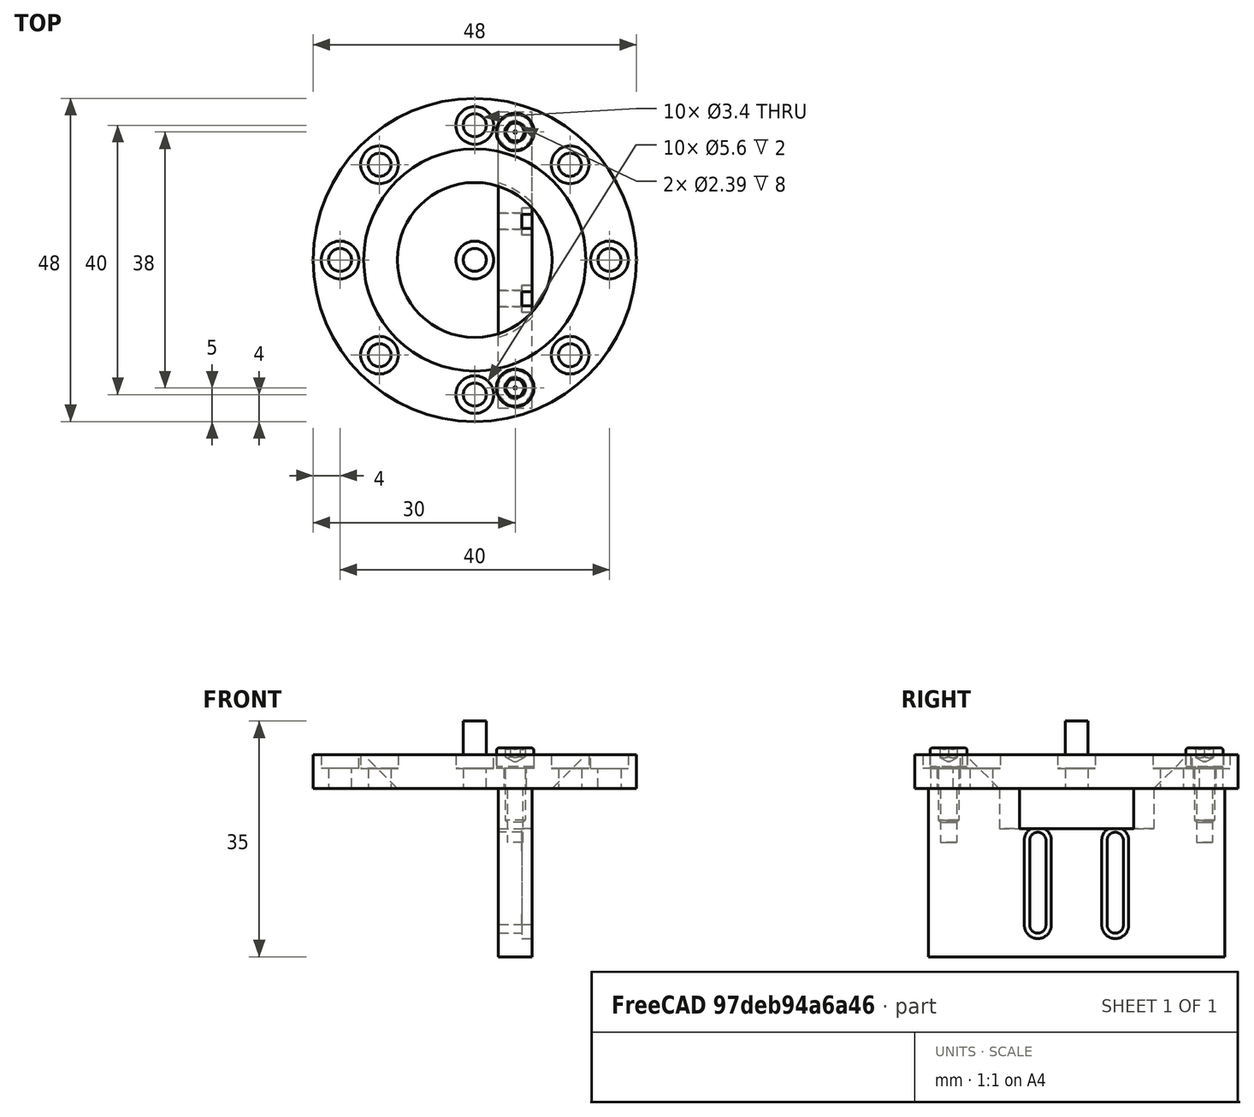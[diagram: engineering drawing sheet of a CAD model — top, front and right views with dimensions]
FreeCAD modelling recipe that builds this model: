
FCSTD DOCUMENT  (FreeCAD 0.22R0.21.2)
Label: PhilipsXL30_AligningRing
License: All rights reserved
LicenseURL: http://en.wikipedia.org/wiki/All_rights_reserved
objects: TechDraw::DrawViewDimension×43, Part::Cylinder×18, Part::MultiFuse×9, TechDraw::DrawProjGroupItem×8, Part::Cut×7, Part::Box×5, Part::FeaturePython×3, TechDraw::DrawSVGTemplate×3, TechDraw::DrawViewSection×3, TechDraw::DrawPage×3, Part::Feature×2, TechDraw::DrawProjGroup×2, TechDraw::DrawViewPart×2, Part::Cone×1
note: 107 computed .brp shape members not serialized (recipe doc carries the construction recipe); baked Part::Feature solids carry a one-line shape summary decoded from their .brp

FEATURE [Part::Cone] Cone001
  Angle = 360
  AttacherType = Attacher::AttachEngine3D
  Height = 20
  Placement = pos=(0,0,-5) rot=(0,0,1;0rad)
  Radius1 = 6.5
  Radius2 = 26.5
FEATURE [Part::Cylinder] Cylinder
  Angle = 360
  AttacherType = Attacher::AttachEngine3D
  FirstAngle = 0
  Height = 5
  Radius = 24
  SecondAngle = 0
FEATURE [Part::Cut] Cut
  Base = -> Cylinder
  Tool = -> Cone001
FEATURE [Part::Box] Box  label="Cube"
  AttacherType = Attacher::AttachEngine3D
  Height = 25
  Length = 5
  Placement = pos=(3.5,-22,-25) rot=(0,0,1;0rad)
  Width = 44
FEATURE [Part::Cylinder] Cylinder001
  Angle = 360
  AttacherType = Attacher::AttachEngine3D
  FirstAngle = 0
  Height = 10
  Radius = 1.2
  SecondAngle = 0
FEATURE [Part::Cylinder] Cylinder002
  Angle = 360
  AttacherType = Attacher::AttachEngine3D
  FirstAngle = 0
  Height = 10
  Placement = pos=(12.6,0,0) rot=(0,0,1;0rad)
  Radius = 1.2
  SecondAngle = 0
FEATURE [Part::Box] Box001  label="Cube001"
  AttacherType = Attacher::AttachEngine3D
  Height = 10
  Length = 12.5
  Placement = pos=(0,-1.2,0) rot=(0,0,1;0rad)
  Width = 2.4
FEATURE [Part::MultiFuse] Fusion  label="Langloch"
  Placement = pos=(0,5.75,-7.7) rot=(0,1,0;1.5708rad)
  Shapes = -> [Box001,Cylinder001,Cylinder002]
FEATURE [Part::Box] Box002  label="Cube002"
  AttacherType = Attacher::AttachEngine3D
  Height = 10
  Length = 12.5
  Placement = pos=(0,-1.2,0) rot=(0,0,1;0rad)
  Width = 2.4
FEATURE [Part::Cylinder] Cylinder003
  Angle = 360
  AttacherType = Attacher::AttachEngine3D
  FirstAngle = 0
  Height = 10
  Radius = 1.2
  SecondAngle = 0
FEATURE [Part::Cylinder] Cylinder004
  Angle = 360
  AttacherType = Attacher::AttachEngine3D
  FirstAngle = 0
  Height = 10
  Placement = pos=(12.6,0,0) rot=(0,0,1;0rad)
  Radius = 1.2
  SecondAngle = 0
FEATURE [Part::MultiFuse] Fusion001  label="Langloch001"
  Placement = pos=(0,-5.75,-7.7) rot=(0,1,0;1.5708rad)
  Shapes = -> [Box002,Cylinder003,Cylinder004]
FEATURE [Part::MultiFuse] Fusion002
  Shapes = -> [Fusion001,Fusion]
FEATURE [Part::Cut] Cut001
  Base = -> Box
  Tool = -> Fusion002
FEATURE [Part::Cylinder] Cylinder005
  Angle = 360
  AttacherType = Attacher::AttachEngine3D
  FirstAngle = 0
  Height = 17
  Placement = pos=(0,0,-6) rot=(0,0,1;0rad)
  Radius = 12
  SecondAngle = 0
FEATURE [Part::Cut] Cut002
  Base = -> Cut001
  Tool = -> Cylinder005
FEATURE [Part::FeaturePython] Screw  label="M3x8-Screw"  # Fasteners workbench fastener (typed FeaturePython)
  Placement = pos=(6,19,3) rot=(0,0,1;0rad)
  diameter = 4
  invert = false
  leftHanded = false
  length = 2
  lengthCustom = 8
  matchOuter = false
  offset = 0
  thread = false
  type = 48
FEATURE [Part::FeaturePython] Screw001  label="M3x8-Screw001"  # Fasteners workbench fastener (typed FeaturePython)
  Placement = pos=(6,-19,3) rot=(0,0,1;0rad)
  diameter = 4
  invert = false
  leftHanded = false
  length = 2
  lengthCustom = 8
  matchOuter = false
  offset = 0
  thread = false
  type = 48
FEATURE [Part::Cylinder] Cylinder006
  Angle = 360
  AttacherType = Attacher::AttachEngine3D
  FirstAngle = 0
  Height = 10
  Placement = pos=(6,19,-8) rot=(0,0,1;0rad)
  Radius = 1.195
  SecondAngle = 0
FEATURE [Part::Cylinder] Cylinder007
  Angle = 360
  AttacherType = Attacher::AttachEngine3D
  FirstAngle = 0
  Height = 10
  Placement = pos=(6,-19,-8) rot=(0,0,1;0rad)
  Radius = 1.195
  SecondAngle = 0
FEATURE [Part::MultiFuse] Fusion003
  Shapes = -> [Cylinder006,Cylinder007]
FEATURE [Part::Cut] Cut003  label="Kickeraligner_01"
  Base = -> Cut002
  Tool = -> Fusion003
FEATURE [Part::Cylinder] Cylinder008
  Angle = 360
  AttacherType = Attacher::AttachEngine3D
  FirstAngle = 0
  Height = 10
  Placement = pos=(6,19,0) rot=(0,0,1;0rad)
  Radius = 1.7
  SecondAngle = 0
FEATURE [Part::Cylinder] Cylinder009
  Angle = 360
  AttacherType = Attacher::AttachEngine3D
  FirstAngle = 0
  Height = 10
  Placement = pos=(6,-19,0) rot=(0,0,1;0rad)
  Radius = 1.7
  SecondAngle = 0
FEATURE [Part::Cylinder] Cylinder010
  Angle = 360
  AttacherType = Attacher::AttachEngine3D
  FirstAngle = 0
  Height = 2
  Placement = pos=(6,19,3) rot=(0,0,1;0rad)
  Radius = 2.8
  SecondAngle = 0
FEATURE [Part::Cylinder] Cylinder011
  Angle = 360
  AttacherType = Attacher::AttachEngine3D
  FirstAngle = 0
  Height = 2
  Placement = pos=(6,-19,3) rot=(0,0,1;0rad)
  Radius = 2.8
  SecondAngle = 0
FEATURE [Part::MultiFuse] Fusion004
  Shapes = -> [Cylinder008,Cylinder009,Cylinder010,Cylinder011]
FEATURE [Part::Cut] Cut004
  Base = -> Cut
  Tool = -> Fusion004
FEATURE [Part::Cylinder] Cylinder012
  Angle = 360
  AttacherType = Attacher::AttachEngine3D
  FirstAngle = 0
  Height = 2
  Placement = pos=(0,0,3) rot=(0,0,1;0rad)
  Radius = 2.8
  SecondAngle = 0
FEATURE [Part::Cylinder] Cylinder013
  Angle = 360
  AttacherType = Attacher::AttachEngine3D
  FirstAngle = 0
  Height = 10
  Radius = 1.7
  SecondAngle = 0
FEATURE [Part::MultiFuse] Fusion005
  Shapes = -> [Cylinder013,Cylinder012]
FEATURE [Part::FeaturePython] Array  # Draft array (typed FeaturePython)
  AlwaysSyncPlacement = false
  Angle = 360
  ArrayType = 2
  Axis = (0,0,1)
  Base = -> Fusion005
  Center = (0,0,0)
  Count = 9
  ExpandArray = false
  Fuse = false
  IntervalAxis = (0,0,0)
  IntervalX = (100,0,0)
  IntervalY = (0,100,0)
  IntervalZ = (0,0,100)
  NumberCircles = 2
  NumberPolar = 5
  NumberX = 2
  NumberY = 2
  NumberZ = 1
  PlacementList = 9 placements: [(0,0,0),(-20,0,0),(-14.1421,-14.1421,0),(-4.44089e-15,-20,0),(14.1421,-14.1421,0),(20,-2.44929e-15,0),(14.1421,14.1421,0),(4.44089e-15,20,0),(-14.1421,14.1421,0)]
  RadialDistance = 20
  ScaleList = (9) [(1,1,1),(1,1,1),(1,1,1),(1,1,1),(1,1,1),(1,1,1),(1,1,1),(1,1,1),(1,1,1)]
  Symmetry = 1
  TangentialDistance = 15
FEATURE [Part::Cut] Cut005  label="AligningRing"
  Base = -> Cut004
  Tool = -> Array
FEATURE [Part::Feature] Cut005_solid  label="AligningRing (Solid)"
  shape: bbox 48 x 48 x 5 mm, 34 faces (baked)
FEATURE [TechDraw::DrawSVGTemplate] Template
  EditableTexts = Designed_by_Name=Thomas Spielauer; FC-Date=2024-06-04; FC-SC=mm; FC-Title=XL30 Column Alignment Ring; Subtitle=Subtitle
  Height = 210
  Orientation = 1
  Template = <path>
  Width = 297
FEATURE [TechDraw::DrawProjGroupItem] ProjItem  label="Front"
  CoarseView = false
  Direction = (0,0,1)
  Focus = 100
  HardHidden = false
  IsoCount = 0
  IsoHidden = false
  IsoVisible = false
  LockPosition = true
  Perspective = false
  Rotation = 0
  RotationVector = (0,1,0)
  Scale = 2
  ScaleType = 2
  ScrubCount = 0
  SeamHidden = false
  SeamVisible = false
  SmoothHidden = false
  SmoothVisible = true
  Source = -> [Cut005]
  Type = 0
  X = 0
  XDirection = (0,1,0)
  Y = 0
FEATURE [TechDraw::DrawProjGroupItem] ProjItem001  label="Rear"
  CoarseView = false
  Direction = (0,0,-1)
  Focus = 100
  HardHidden = false
  IsoCount = 0
  IsoHidden = false
  IsoVisible = false
  LockPosition = false
  Perspective = false
  Rotation = 0
  RotationVector = (1,0,0)
  Scale = 2
  ScaleType = 2
  ScrubCount = 0
  SeamHidden = false
  SeamVisible = false
  SmoothHidden = false
  SmoothVisible = true
  Source = -> [Cut005]
  Type = 3
  X = 136
  XDirection = (0,-1,0)
  Y = 0
FEATURE [TechDraw::DrawProjGroupItem] ProjItem002  label="Left"
  CoarseView = false
  Direction = (0,-1,1e-16)
  Focus = 100
  HardHidden = false
  IsoCount = 0
  IsoHidden = false
  IsoVisible = false
  LockPosition = false
  Perspective = false
  Rotation = 0
  RotationVector = (1,0,0)
  Scale = 2
  ScaleType = 2
  ScrubCount = 0
  SeamHidden = false
  SeamVisible = false
  SmoothHidden = false
  SmoothVisible = true
  Source = -> [Cut005]
  Type = 1
  X = 68
  XDirection = (0,1e-16,1)
  Y = 0
FEATURE [TechDraw::DrawProjGroup] ProjGroup
  Anchor = -> ProjItem
  AutoDistribute = true
  LockPosition = false
  ProjectionType = 0
  Rotation = 0
  Scale = 2
  ScaleType = 1
  Source = -> [Cut005]
  Views = -> [ProjItem,ProjItem001,ProjItem002]
  X = 75.1959
  Y = 130.904
  spacingX = 15
  spacingY = 15
FEATURE [TechDraw::DrawViewDimension] Dimension
  AngleOverride = false
  Arbitrary = false
  ArbitraryTolerances = false
  EqualTolerance = true
  ExtensionAngle = 0
  FormatSpec = %.2w
  FormatSpecOverTolerance = %+.2w
  FormatSpecUnderTolerance = %+.2w
  Inverted = false
  LineAngle = 0
  LockPosition = false
  MeasureType = 1
  OverTolerance = 0
  References2D = -> [ProjItem002]
  Rotation = 0
  ScaleType = 0
  TheoreticalExact = false
  Type = 1
  UnderTolerance = 0
  X = 14.6766
  Y = 64.1241
FEATURE [TechDraw::DrawViewDimension] Dimension001
  AngleOverride = false
  Arbitrary = false
  ArbitraryTolerances = false
  EqualTolerance = true
  ExtensionAngle = 0
  FormatSpec = ⌀%.2w
  FormatSpecOverTolerance = %+.2w
  FormatSpecUnderTolerance = %+.2w
  Inverted = false
  LineAngle = 0
  LockPosition = false
  MeasureType = 1
  OverTolerance = 0
  References2D = -> [ProjItem001]
  Rotation = 0
  ScaleType = 0
  TheoreticalExact = false
  Type = 5
  UnderTolerance = 0
  X = 14.4966
  Y = 59.5959
FEATURE [TechDraw::DrawViewDimension] Dimension002
  AngleOverride = false
  Arbitrary = false
  ArbitraryTolerances = false
  EqualTolerance = true
  ExtensionAngle = 0
  FormatSpec = ⌀%.2w
  FormatSpecOverTolerance = %+.2w
  FormatSpecUnderTolerance = %+.2w
  Inverted = false
  LineAngle = 0
  LockPosition = false
  MeasureType = 1
  OverTolerance = 0
  References2D = -> [ProjItem001]
  Rotation = 0
  ScaleType = 0
  TheoreticalExact = false
  Type = 5
  UnderTolerance = 0
  X = 30.1939
  Y = 53.0714
FEATURE [TechDraw::DrawViewDimension] Dimension003
  AngleOverride = false
  Arbitrary = false
  ArbitraryTolerances = false
  EqualTolerance = true
  ExtensionAngle = 0
  FormatSpec = ⌀%.2w (10x)
  FormatSpecOverTolerance = %+.2w
  FormatSpecUnderTolerance = %+.2w
  Inverted = false
  LineAngle = 0
  LockPosition = false
  MeasureType = 1
  OverTolerance = 0
  References2D = -> [ProjItem001]
  Rotation = 0
  ScaleType = 0
  TheoreticalExact = false
  Type = 5
  UnderTolerance = 0
  X = 49.7609
  Y = 51.7571
FEATURE [TechDraw::DrawViewDimension] Dimension004
  AngleOverride = false
  Arbitrary = false
  ArbitraryTolerances = false
  EqualTolerance = true
  ExtensionAngle = 0
  FormatSpec = ⌀%.2w
  FormatSpecOverTolerance = %+.2w
  FormatSpecUnderTolerance = %+.2w
  Inverted = false
  LineAngle = 0
  LockPosition = false
  MeasureType = 1
  OverTolerance = 0
  References2D = -> [ProjItem]
  Rotation = 0
  ScaleType = 0
  TheoreticalExact = false
  Type = 5
  UnderTolerance = 0
  X = 33.9204
  Y = 57.7895
FEATURE [TechDraw::DrawViewDimension] Dimension005
  AngleOverride = false
  Arbitrary = false
  ArbitraryTolerances = false
  EqualTolerance = true
  ExtensionAngle = 0
  FormatSpec = ⌀%.2w
  FormatSpecOverTolerance = %+.2w
  FormatSpecUnderTolerance = %+.2w
  Inverted = false
  LineAngle = 0
  LockPosition = false
  MeasureType = 1
  OverTolerance = 0
  References2D = -> [ProjItem]
  Rotation = 0
  ScaleType = 0
  TheoreticalExact = false
  Type = 5
  UnderTolerance = 0
  X = 26.899
  Y = 61.6719
FEATURE [TechDraw::DrawViewDimension] Dimension006
  AngleOverride = false
  Arbitrary = false
  ArbitraryTolerances = false
  EqualTolerance = true
  ExtensionAngle = 0
  FormatSpec = ⌀%.2w
  FormatSpecOverTolerance = %+.2w
  FormatSpecUnderTolerance = %+.2w
  Inverted = false
  LineAngle = 0
  LockPosition = false
  MeasureType = 1
  OverTolerance = 0
  References2D = -> [ProjItem]
  Rotation = 0
  ScaleType = 0
  TheoreticalExact = false
  Type = 5
  UnderTolerance = 0
  X = 17.5465
  Y = 63.697
FEATURE [TechDraw::DrawViewDimension] Dimension007
  AngleOverride = false
  Arbitrary = false
  ArbitraryTolerances = false
  EqualTolerance = true
  ExtensionAngle = 0
  FormatSpec = ⌀%.2w (10x)
  FormatSpecOverTolerance = %+.2w
  FormatSpecUnderTolerance = %+.2w
  Inverted = false
  LineAngle = 0
  LockPosition = false
  MeasureType = 1
  OverTolerance = 0
  References2D = -> [ProjItem]
  Rotation = 0
  ScaleType = 0
  TheoreticalExact = false
  Type = 5
  UnderTolerance = 0
  X = 45.3319
  Y = 51.7849
FEATURE [TechDraw::DrawViewDimension] Dimension008
  AngleOverride = false
  Arbitrary = false
  ArbitraryTolerances = false
  EqualTolerance = true
  ExtensionAngle = 0
  FormatSpec = ⌀%.2w
  FormatSpecOverTolerance = %+.2w
  FormatSpecUnderTolerance = %+.2w
  Inverted = false
  LineAngle = 0
  LockPosition = false
  MeasureType = 1
  OverTolerance = 0
  References2D = -> [ProjItem]
  Rotation = 0
  ScaleType = 0
  TheoreticalExact = false
  Type = 5
  UnderTolerance = 0
  X = -16.0753
  Y = 61.592
FEATURE [TechDraw::DrawViewDimension] Dimension009
  AngleOverride = false
  Arbitrary = false
  ArbitraryTolerances = false
  EqualTolerance = true
  ExtensionAngle = 0
  FormatSpec = %.2w (8x)
  FormatSpecOverTolerance = %+.2w
  FormatSpecUnderTolerance = %+.2w
  Inverted = false
  LineAngle = 0
  LockPosition = false
  MeasureType = 1
  OverTolerance = 0
  References2D = -> [ProjItem]
  Rotation = 0
  ScaleType = 0
  TheoreticalExact = false
  Type = 6
  UnderTolerance = 0
  X = -52.7672
  Y = 29.4701
FEATURE [TechDraw::DrawViewDimension] Dimension010
  AngleOverride = false
  Arbitrary = false
  ArbitraryTolerances = false
  EqualTolerance = true
  ExtensionAngle = 0
  FormatSpec = %.2w (2x)
  FormatSpecOverTolerance = %+.2w
  FormatSpecUnderTolerance = %+.2w
  Inverted = false
  LineAngle = 0
  LockPosition = false
  MeasureType = 1
  OverTolerance = 0
  References2D = -> [ProjItem]
  Rotation = 0
  ScaleType = 0
  TheoreticalExact = false
  Type = 6
  UnderTolerance = 0
  X = -41.0402
  Y = -30.1439
FEATURE [TechDraw::DrawViewSection] SectionView  label="Section  - "
  BaseView = -> ProjItem
  CoarseView = false
  CutSurfaceDisplay = 2
  Direction = (1e-16,-1,0)
  FileGeomPattern = <path>
  FileHatchPattern = <path>
  Focus = 100
  FuseBeforeCut = false
  HardHidden = false
  HatchOffset = (0,0,0)
  HatchRotation = 0
  HatchScale = 1
  IsoCount = 0
  IsoHidden = false
  IsoVisible = false
  LockPosition = false
  NameGeomPattern = Diamond
  Perspective = false
  Rotation = 0
  Scale = 2
  ScaleType = 2
  ScrubCount = 0
  SeamHidden = false
  SeamVisible = false
  SectionDirection = 4
  SectionLineStretch = 1
  SectionNormal = (1e-16,-1,0)
  SectionOrigin = (0,0,2.5)
  SmoothHidden = false
  SmoothVisible = true
  Source = -> [Cut005]
  TrimAfterCut = false
  UsePreviousCut = false
  X = 78.0601
  XDirection = (1,1e-16,0)
  Y = 34.3268
FEATURE [TechDraw::DrawViewDimension] Dimension011
  AngleOverride = false
  Arbitrary = false
  ArbitraryTolerances = false
  EqualTolerance = true
  ExtensionAngle = 0
  FormatSpec = %.2w
  FormatSpecOverTolerance = %+.2w
  FormatSpecUnderTolerance = %+.2w
  Inverted = false
  LineAngle = 0
  LockPosition = false
  MeasureType = 1
  OverTolerance = 0
  References2D = -> [SectionView]
  Rotation = 0
  ScaleType = 0
  TheoreticalExact = false
  Type = 2
  UnderTolerance = 0
  X = -56.9152
  Y = 17.9756
FEATURE [TechDraw::DrawViewDimension] Dimension012
  AngleOverride = false
  Arbitrary = false
  ArbitraryTolerances = false
  EqualTolerance = true
  ExtensionAngle = 0
  FormatSpec = %.2w
  FormatSpecOverTolerance = %+.2w
  FormatSpecUnderTolerance = %+.2w
  Inverted = false
  LineAngle = 0
  LockPosition = false
  MeasureType = 1
  OverTolerance = 0
  References2D = -> [SectionView]
  Rotation = 0
  ScaleType = 0
  TheoreticalExact = false
  Type = 2
  UnderTolerance = 0
  X = 51.4914
  Y = 16.9401
FEATURE [TechDraw::DrawViewDimension] Dimension013
  AngleOverride = false
  Arbitrary = false
  ArbitraryTolerances = false
  EqualTolerance = true
  ExtensionAngle = 0
  FormatSpec = %.2w
  FormatSpecOverTolerance = %+.2w
  FormatSpecUnderTolerance = %+.2w
  Inverted = false
  LineAngle = 0
  LockPosition = false
  MeasureType = 1
  OverTolerance = 0
  References2D = -> [SectionView]
  Rotation = 0
  ScaleType = 0
  TheoreticalExact = false
  Type = 1
  UnderTolerance = 0
  X = -1.79985
  Y = 16.369
FEATURE [TechDraw::DrawViewDimension] Dimension014
  AngleOverride = false
  Arbitrary = false
  ArbitraryTolerances = false
  EqualTolerance = true
  ExtensionAngle = 0
  FormatSpec = %.2w
  FormatSpecOverTolerance = %+.2w
  FormatSpecUnderTolerance = %+.2w
  Inverted = false
  LineAngle = 0
  LockPosition = false
  MeasureType = 1
  OverTolerance = 0
  References2D = -> [SectionView]
  Rotation = 0
  ScaleType = 0
  TheoreticalExact = false
  Type = 1
  UnderTolerance = 0
  X = -1.61231
  Y = -11.4713
FEATURE [TechDraw::DrawViewDimension] Dimension016
  AngleOverride = false
  Arbitrary = false
  ArbitraryTolerances = false
  EqualTolerance = true
  ExtensionAngle = 0
  FormatSpec = %.2w
  FormatSpecOverTolerance = %+.2w
  FormatSpecUnderTolerance = %+.2w
  Inverted = false
  LineAngle = 0
  LockPosition = false
  MeasureType = 1
  OverTolerance = 0
  References2D = -> [SectionView]
  Rotation = 0
  ScaleType = 0
  TheoreticalExact = false
  Type = 1
  UnderTolerance = 0
  X = -50.6255
  Y = -9.92308
FEATURE [TechDraw::DrawViewDimension] Dimension017
  AngleOverride = false
  Arbitrary = false
  ArbitraryTolerances = false
  EqualTolerance = true
  ExtensionAngle = 0
  FormatSpec = %.2w
  FormatSpecOverTolerance = %+.2w
  FormatSpecUnderTolerance = %+.2w
  Inverted = false
  LineAngle = 0
  LockPosition = false
  MeasureType = 1
  OverTolerance = 0
  References2D = -> [SectionView]
  Rotation = 0
  ScaleType = 0
  TheoreticalExact = false
  Type = 1
  UnderTolerance = 0
  X = -39.3802
  Y = 21.6146
FEATURE [TechDraw::DrawViewDimension] Dimension018
  AngleOverride = false
  Arbitrary = false
  ArbitraryTolerances = false
  EqualTolerance = true
  ExtensionAngle = 0
  FormatSpec = %.2w
  FormatSpecOverTolerance = %+.2w
  FormatSpecUnderTolerance = %+.2w
  Inverted = false
  LineAngle = 0
  LockPosition = false
  MeasureType = 1
  OverTolerance = 0
  References2D = -> [SectionView]
  Rotation = 0
  ScaleType = 0
  TheoreticalExact = false
  Type = 6
  UnderTolerance = 0
  X = 23.2977
  Y = -7.15191
FEATURE [TechDraw::DrawPage] Page
  KeepUpdated = true
  NextBalloonIndex = 1
  ProjectionType = 0
  Template = -> Template
  Views = -> [ProjGroup,Dimension,Dimension001,Dimension002,Dimension003,Dimension004,Dimension005,Dimension006,Dimension007,Dimension008,Dimension009,Dimension010,SectionView,Dimension011,Dimension012,Dimension013,Dimension014,Dimension016,Dimension017,Dimension018]
FEATURE [TechDraw::DrawSVGTemplate] Template001
  EditableTexts = Designed_by_Name=Thomas Spielauer; FC-Date=2024-06-04; FC-SC=mm; FC-Title=XL30 Kicker v3 Aligner; Subtitle=for Column aligning ring
  Height = 210
  Orientation = 1
  Template = <path>
  Width = 297
FEATURE [Part::Box] Box003  label="Cube003"
  AttacherType = Attacher::AttachEngine3D
  Height = 1.6
  Length = 12.5
  Placement = pos=(0,-2,0) rot=(0,0,1;0rad)
  Width = 4
FEATURE [Part::Cylinder] Cylinder014
  Angle = 360
  AttacherType = Attacher::AttachEngine3D
  FirstAngle = 0
  Height = 1.6
  Radius = 2
  SecondAngle = 0
FEATURE [Part::Cylinder] Cylinder015
  Angle = 360
  AttacherType = Attacher::AttachEngine3D
  FirstAngle = 0
  Height = 1.6
  Placement = pos=(12.6,0,0) rot=(0,0,1;0rad)
  Radius = 2
  SecondAngle = 0
FEATURE [Part::MultiFuse] Fusion006  label="Langloch002"
  Placement = pos=(7,-5.75,-7.7) rot=(0,1,0;1.5708rad)
  Shapes = -> [Box003,Cylinder014,Cylinder015]
FEATURE [Part::Box] Box004  label="Cube004"
  AttacherType = Attacher::AttachEngine3D
  Height = 1.6
  Length = 12.5
  Placement = pos=(0,-2,0) rot=(0,0,1;0rad)
  Width = 4
FEATURE [Part::Cylinder] Cylinder016
  Angle = 360
  AttacherType = Attacher::AttachEngine3D
  FirstAngle = 0
  Height = 1.6
  Radius = 2
  SecondAngle = 0
FEATURE [Part::Cylinder] Cylinder017
  Angle = 360
  AttacherType = Attacher::AttachEngine3D
  FirstAngle = 0
  Height = 1.6
  Placement = pos=(12.6,0,0) rot=(0,0,1;0rad)
  Radius = 2
  SecondAngle = 0
FEATURE [Part::MultiFuse] Fusion007  label="Langloch003"
  Placement = pos=(7,5.75,-7.7) rot=(0,1,0;1.5708rad)
  Shapes = -> [Box004,Cylinder016,Cylinder017]
FEATURE [Part::MultiFuse] Fusion008
  Shapes = -> [Fusion007,Fusion006]
FEATURE [Part::Cut] Cut006  label="Kickeraligner"
  Base = -> Cut003
  Tool = -> Fusion008
FEATURE [Part::Feature] Cut006_solid  label="Kickeraligner (Solid)"
  shape: bbox 5 x 44 x 25 mm, 60 faces (baked)
FEATURE [TechDraw::DrawProjGroupItem] ProjItem003  label="Front001"
  CoarseView = false
  Direction = (1,0,0)
  Focus = 100
  HardHidden = false
  IsoCount = 0
  IsoHidden = false
  IsoVisible = false
  LockPosition = true
  Perspective = false
  Rotation = 0
  RotationVector = (0,-1,0)
  Scale = 1.5
  ScaleType = 2
  ScrubCount = 0
  SeamHidden = false
  SeamVisible = false
  SmoothHidden = false
  SmoothVisible = true
  Source = -> [Cut006_solid]
  Type = 0
  X = 0
  XDirection = (0,-1,0)
  Y = 0
FEATURE [TechDraw::DrawProjGroupItem] ProjItem004  label="Bottom"
  CoarseView = false
  Direction = (0,0,1)
  Focus = 100
  HardHidden = false
  IsoCount = 0
  IsoHidden = false
  IsoVisible = false
  LockPosition = false
  Perspective = false
  Rotation = 0
  RotationVector = (1,0,0)
  Scale = 1.5
  ScaleType = 2
  ScrubCount = 0
  SeamHidden = false
  SeamVisible = false
  SmoothHidden = false
  SmoothVisible = true
  Source = -> [Cut006_solid]
  Type = 5
  X = 0
  XDirection = (0,-1,0)
  Y = 59.7197
FEATURE [TechDraw::DrawProjGroupItem] ProjItem005  label="Top"
  CoarseView = false
  Direction = (0,0,-1)
  Focus = 100
  HardHidden = false
  IsoCount = 0
  IsoHidden = false
  IsoVisible = false
  LockPosition = false
  Perspective = false
  Rotation = 0
  RotationVector = (1,0,0)
  Scale = 1.5
  ScaleType = 2
  ScrubCount = 0
  SeamHidden = false
  SeamVisible = false
  SmoothHidden = false
  SmoothVisible = true
  Source = -> [Cut006_solid]
  Type = 4
  X = 0
  XDirection = (0,-1,0)
  Y = -66.6557
FEATURE [TechDraw::DrawProjGroupItem] ProjItem006  label="Left001"
  CoarseView = false
  Direction = (1e-16,1,0)
  Focus = 100
  HardHidden = false
  IsoCount = 0
  IsoHidden = false
  IsoVisible = false
  LockPosition = false
  Perspective = false
  Rotation = 0
  RotationVector = (1,0,0)
  Scale = 1.5
  ScaleType = 2
  ScrubCount = 0
  SeamHidden = false
  SeamVisible = false
  SmoothHidden = false
  SmoothVisible = true
  Source = -> [Cut006_solid]
  Type = 1
  X = 84.3121
  XDirection = (1,-1e-16,0)
  Y = 0
FEATURE [TechDraw::DrawProjGroupItem] ProjItem007  label="Rear001"
  CoarseView = false
  Direction = (-1,0,0)
  Focus = 100
  HardHidden = false
  IsoCount = 0
  IsoHidden = false
  IsoVisible = false
  LockPosition = false
  Perspective = false
  Rotation = 0
  RotationVector = (1,0,0)
  Scale = 1.5
  ScaleType = 2
  ScrubCount = 0
  SeamHidden = false
  SeamVisible = false
  SmoothHidden = false
  SmoothVisible = true
  Source = -> [Cut006_solid]
  Type = 3
  X = 151.913
  XDirection = (0,1,0)
  Y = 0
FEATURE [TechDraw::DrawProjGroup] ProjGroup001
  Anchor = -> ProjItem003
  AutoDistribute = false
  LockPosition = false
  ProjectionType = 0
  Rotation = 0
  Scale = 1.5
  ScaleType = 1
  Source = -> [Cut006_solid]
  Views = -> [ProjItem003,ProjItem004,ProjItem005,ProjItem006,ProjItem007]
  X = 71.7176
  Y = 109.819
  spacingX = 15
  spacingY = 15
FEATURE [TechDraw::DrawViewDimension] Dimension019
  AngleOverride = false
  Arbitrary = false
  ArbitraryTolerances = false
  EqualTolerance = true
  ExtensionAngle = 0
  FormatSpec = %.2w
  FormatSpecOverTolerance = %+.2w
  FormatSpecUnderTolerance = %+.2w
  Inverted = false
  LineAngle = 0
  LockPosition = false
  MeasureType = 1
  OverTolerance = 0
  References2D = -> [ProjItem005]
  Rotation = 0
  ScaleType = 0
  TheoreticalExact = false
  Type = 0
  UnderTolerance = 0
  X = -2.74227
  Y = 17.7496
FEATURE [TechDraw::DrawViewDimension] Dimension020
  AngleOverride = false
  Arbitrary = false
  ArbitraryTolerances = false
  EqualTolerance = true
  ExtensionAngle = 0
  FormatSpec = %.2w
  FormatSpecOverTolerance = %+.2w
  FormatSpecUnderTolerance = %+.2w
  Inverted = false
  LineAngle = 0
  LockPosition = false
  MeasureType = 1
  OverTolerance = 0
  References2D = -> [ProjItem005]
  Rotation = 0
  ScaleType = 0
  TheoreticalExact = false
  Type = 0
  UnderTolerance = 0
  X = -42.4052
  Y = 17.6073
FEATURE [TechDraw::DrawViewDimension] Dimension021
  AngleOverride = false
  Arbitrary = false
  ArbitraryTolerances = false
  EqualTolerance = true
  ExtensionAngle = 0
  FormatSpec = %.2w
  FormatSpecOverTolerance = %+.2w
  FormatSpecUnderTolerance = %+.2w
  Inverted = false
  LineAngle = 0
  LockPosition = false
  MeasureType = 1
  OverTolerance = 0
  References2D = -> [ProjItem004]
  Rotation = 0
  ScaleType = 0
  TheoreticalExact = false
  Type = 0
  UnderTolerance = 0
  X = 38.6315
  Y = 21.9645
FEATURE [TechDraw::DrawViewDimension] Dimension022
  AngleOverride = false
  Arbitrary = false
  ArbitraryTolerances = false
  EqualTolerance = true
  ExtensionAngle = 0
  FormatSpec = %.2w
  FormatSpecOverTolerance = %+.2w
  FormatSpecUnderTolerance = %+.2w
  Inverted = false
  LineAngle = 0
  LockPosition = false
  MeasureType = 1
  OverTolerance = 0
  References2D = -> [ProjItem004]
  Rotation = 0
  ScaleType = 0
  TheoreticalExact = false
  Type = 0
  UnderTolerance = 0
  X = 44.0976
  Y = 10.1057
FEATURE [TechDraw::DrawViewDimension] Dimension023
  AngleOverride = false
  Arbitrary = false
  ArbitraryTolerances = false
  EqualTolerance = true
  ExtensionAngle = 0
  FormatSpec = ⌀%.2w (2x M3)
  FormatSpecOverTolerance = %+.2w
  FormatSpecUnderTolerance = %+.2w
  Inverted = false
  LineAngle = 0
  LockPosition = false
  MeasureType = 1
  OverTolerance = 0
  References2D = -> [ProjItem004]
  Rotation = 0
  ScaleType = 0
  TheoreticalExact = false
  Type = 5
  UnderTolerance = 0
  X = -49.8518
  Y = -22.963
FEATURE [TechDraw::DrawViewDimension] Dimension024
  AngleOverride = false
  Arbitrary = false
  ArbitraryTolerances = false
  EqualTolerance = true
  ExtensionAngle = 0
  FormatSpec = %.2w
  FormatSpecOverTolerance = %+.2w
  FormatSpecUnderTolerance = %+.2w
  Inverted = false
  LineAngle = 0
  LockPosition = false
  MeasureType = 1
  OverTolerance = 0
  References2D = -> [ProjItem003]
  Rotation = 0
  ScaleType = 0
  TheoreticalExact = false
  Type = 0
  UnderTolerance = 0
  X = 26.1719
  Y = 34.0957
FEATURE [TechDraw::DrawViewDimension] Dimension025
  AngleOverride = false
  Arbitrary = false
  ArbitraryTolerances = false
  EqualTolerance = true
  ExtensionAngle = 0
  FormatSpec = %.2w
  FormatSpecOverTolerance = %+.2w
  FormatSpecUnderTolerance = %+.2w
  Inverted = false
  LineAngle = 0
  LockPosition = false
  MeasureType = 1
  OverTolerance = 0
  References2D = -> [ProjItem003]
  Rotation = 0
  ScaleType = 0
  TheoreticalExact = false
  Type = 0
  UnderTolerance = 0
  X = 29.3359
  Y = 42.2976
FEATURE [TechDraw::DrawViewDimension] Dimension026
  AngleOverride = false
  Arbitrary = false
  ArbitraryTolerances = false
  EqualTolerance = true
  ExtensionAngle = 0
  FormatSpec = %.2w
  FormatSpecOverTolerance = %+.2w
  FormatSpecUnderTolerance = %+.2w
  Inverted = false
  LineAngle = 0
  LockPosition = false
  MeasureType = 1
  OverTolerance = 0
  References2D = -> [ProjItem003]
  Rotation = 0
  ScaleType = 0
  TheoreticalExact = false
  Type = 0
  UnderTolerance = 0
  X = 46.3655
  Y = 25.9377
FEATURE [TechDraw::DrawViewDimension] Dimension027
  AngleOverride = false
  Arbitrary = false
  ArbitraryTolerances = false
  EqualTolerance = true
  ExtensionAngle = 0
  FormatSpec = %.2w
  FormatSpecOverTolerance = %+.2w
  FormatSpecUnderTolerance = %+.2w
  Inverted = false
  LineAngle = 0
  LockPosition = false
  MeasureType = 1
  OverTolerance = 0
  References2D = -> [ProjItem003]
  Rotation = 0
  ScaleType = 0
  TheoreticalExact = false
  Type = 0
  UnderTolerance = 0
  X = 40.1856
  Y = 3.86506
FEATURE [TechDraw::DrawViewDimension] Dimension028
  AngleOverride = false
  Arbitrary = false
  ArbitraryTolerances = false
  EqualTolerance = true
  ExtensionAngle = 0
  FormatSpec = %.2w
  FormatSpecOverTolerance = %+.2w
  FormatSpecUnderTolerance = %+.2w
  Inverted = false
  LineAngle = 0
  LockPosition = false
  MeasureType = 1
  OverTolerance = 0
  References2D = -> [ProjItem003]
  Rotation = 0
  ScaleType = 0
  TheoreticalExact = false
  Type = 0
  UnderTolerance = 0
  X = -21.0897
  Y = 32.0725
FEATURE [TechDraw::DrawViewDimension] Dimension029
  AngleOverride = false
  Arbitrary = false
  ArbitraryTolerances = false
  EqualTolerance = true
  ExtensionAngle = 0
  FormatSpec = %.2w
  FormatSpecOverTolerance = %+.2w
  FormatSpecUnderTolerance = %+.2w
  Inverted = false
  LineAngle = 0
  LockPosition = false
  MeasureType = 1
  OverTolerance = 0
  References2D = -> [ProjItem007]
  Rotation = 0
  ScaleType = 0
  TheoreticalExact = false
  Type = 0
  UnderTolerance = 0
  X = 0.798609
  Y = 37.539
FEATURE [TechDraw::DrawViewDimension] Dimension030
  AngleOverride = false
  Arbitrary = false
  ArbitraryTolerances = false
  EqualTolerance = true
  ExtensionAngle = 0
  FormatSpec = %.2w
  FormatSpecOverTolerance = %+.2w
  FormatSpecUnderTolerance = %+.2w
  Inverted = false
  LineAngle = 0
  LockPosition = false
  MeasureType = 1
  OverTolerance = 0
  References2D = -> [ProjItem007]
  Rotation = 0
  ScaleType = 0
  TheoreticalExact = false
  Type = 0
  UnderTolerance = 0
  X = -2.99683
  Y = -30.5721
FEATURE [TechDraw::DrawViewDimension] Dimension031
  AngleOverride = false
  Arbitrary = false
  ArbitraryTolerances = false
  EqualTolerance = true
  ExtensionAngle = 0
  FormatSpec = %.2w
  FormatSpecOverTolerance = %+.2w
  FormatSpecUnderTolerance = %+.2w
  Inverted = false
  LineAngle = 0
  LockPosition = false
  MeasureType = 1
  OverTolerance = 0
  References2D = -> [ProjItem004]
  Rotation = 0
  ScaleType = 0
  TheoreticalExact = false
  Type = 0
  UnderTolerance = 0
  X = -28.8881
  Y = -11.5813
FEATURE [TechDraw::DrawViewDimension] Dimension032
  AngleOverride = false
  Arbitrary = false
  ArbitraryTolerances = false
  EqualTolerance = true
  ExtensionAngle = 0
  FormatSpec = %.2w
  FormatSpecOverTolerance = %+.2w
  FormatSpecUnderTolerance = %+.2w
  Inverted = false
  LineAngle = 0
  LockPosition = false
  MeasureType = 1
  OverTolerance = 0
  References2D = -> [ProjItem004]
  Rotation = 0
  ScaleType = 0
  TheoreticalExact = false
  Type = 0
  UnderTolerance = 0
  X = -1.50669
  Y = 20.5059
FEATURE [TechDraw::DrawPage] Page001
  KeepUpdated = true
  NextBalloonIndex = 1
  ProjectionType = 0
  Template = -> Template001
  Views = -> [ProjGroup001,Dimension019,Dimension020,Dimension021,Dimension022,Dimension023,Dimension024,Dimension025,Dimension026,Dimension027,Dimension028,Dimension029,Dimension030,Dimension031,Dimension032]
FEATURE [TechDraw::DrawSVGTemplate] Template002
  EditableTexts = Designed_by_Name=Designed by Name; Drawing_number=Drawing number; FC-Date=Date; FC-SC=Scale; FC-SH=Sheet; FC-Title=Title; Subtitle=Subtitle; Weight=Weight
  Height = 210
  Orientation = 1
  Template = <path>
  Width = 297
FEATURE [TechDraw::DrawViewPart] View
  CoarseView = false
  Direction = (1,0,0)
  Focus = 100
  HardHidden = false
  IsoCount = 0
  IsoHidden = false
  IsoVisible = false
  LockPosition = false
  Perspective = false
  Rotation = 0
  ScaleType = 0
  ScrubCount = 0
  SeamHidden = false
  SeamVisible = false
  SmoothHidden = false
  SmoothVisible = true
  Source = -> [Cut006_solid]
  X = 213.863
  XDirection = (0,-1,0)
  Y = 154.674
FEATURE [TechDraw::DrawViewPart] View001
  CoarseView = false
  Direction = (1,0,0)
  Focus = 100
  HardHidden = false
  IsoCount = 0
  IsoHidden = false
  IsoVisible = false
  LockPosition = false
  Perspective = false
  Rotation = 0
  ScaleType = 0
  ScrubCount = 0
  SeamHidden = false
  SeamVisible = false
  SmoothHidden = false
  SmoothVisible = true
  Source = -> [Cut006_solid]
  X = 76.3703
  XDirection = (0,-1,0)
  Y = 177.393
FEATURE [TechDraw::DrawViewSection] SectionView001  label="Section001  - "
  BaseView = -> View
  CoarseView = false
  CutSurfaceDisplay = 2
  Direction = (0,-1e-16,-1)
  FileGeomPattern = <path>
  FileHatchPattern = <path>
  Focus = 100
  FuseBeforeCut = false
  HardHidden = false
  HatchOffset = (0,0,0)
  HatchRotation = 0
  HatchScale = 1
  IsoCount = 0
  IsoHidden = false
  IsoVisible = false
  LockPosition = false
  NameGeomPattern = Diamond
  Perspective = false
  Rotation = 0
  Scale = 3
  ScaleType = 2
  ScrubCount = 0
  SeamHidden = false
  SeamVisible = false
  SectionDirection = 4
  SectionLineStretch = 1
  SectionNormal = (0,-1e-16,-1)
  SectionOrigin = (6,0,-12.5)
  SmoothHidden = false
  SmoothVisible = true
  Source = -> [Cut006_solid]
  TrimAfterCut = false
  UsePreviousCut = false
  X = 212.652
  XDirection = (0,-1,1e-16)
  Y = 93.0024
FEATURE [TechDraw::DrawViewDimension] Dimension033
  AngleOverride = false
  Arbitrary = false
  ArbitraryTolerances = false
  EqualTolerance = true
  ExtensionAngle = 0
  FormatSpec = %.2w
  FormatSpecOverTolerance = %+.2w
  FormatSpecUnderTolerance = %+.2w
  Inverted = false
  LineAngle = 0
  LockPosition = false
  MeasureType = 1
  OverTolerance = 0
  References2D = -> [SectionView001]
  Rotation = 0
  ScaleType = 0
  TheoreticalExact = false
  Type = 0
  UnderTolerance = 0
  X = 64.9192
  Y = -25.9707
FEATURE [TechDraw::DrawViewDimension] Dimension034
  AngleOverride = false
  Arbitrary = false
  ArbitraryTolerances = false
  EqualTolerance = true
  ExtensionAngle = 0
  FormatSpec = %.2w
  FormatSpecOverTolerance = %+.2w
  FormatSpecUnderTolerance = %+.2w
  Inverted = false
  LineAngle = 0
  LockPosition = false
  MeasureType = 1
  OverTolerance = 0
  References2D = -> [SectionView001]
  Rotation = 0
  ScaleType = 0
  TheoreticalExact = false
  Type = 0
  UnderTolerance = 0
  X = 66.5714
  Y = 28.6268
FEATURE [TechDraw::DrawViewDimension] Dimension035
  AngleOverride = false
  Arbitrary = false
  ArbitraryTolerances = false
  EqualTolerance = true
  ExtensionAngle = 0
  FormatSpec = %.2w
  FormatSpecOverTolerance = %+.2w
  FormatSpecUnderTolerance = %+.2w
  Inverted = false
  LineAngle = 0
  LockPosition = false
  MeasureType = 1
  OverTolerance = 0
  References2D = -> [SectionView001]
  Rotation = 0
  ScaleType = 0
  TheoreticalExact = false
  Type = 0
  UnderTolerance = 0
  X = 8.62255
  Y = -13.8392
FEATURE [TechDraw::DrawViewDimension] Dimension036
  AngleOverride = false
  Arbitrary = false
  ArbitraryTolerances = false
  EqualTolerance = true
  ExtensionAngle = 0
  FormatSpec = %.2w
  FormatSpecOverTolerance = %+.2w
  FormatSpecUnderTolerance = %+.2w
  Inverted = false
  LineAngle = 0
  LockPosition = false
  MeasureType = 1
  OverTolerance = 0
  References2D = -> [SectionView001]
  Rotation = 0
  ScaleType = 0
  TheoreticalExact = false
  Type = 0
  UnderTolerance = 0
  X = 47.3332
  Y = -18.2954
FEATURE [TechDraw::DrawViewSection] SectionView002  label="Section002  - "
  BaseView = -> View001
  CoarseView = false
  CutSurfaceDisplay = 2
  Direction = (0,-1e-16,-1)
  FileGeomPattern = <path>
  FileHatchPattern = <path>
  Focus = 100
  FuseBeforeCut = false
  HardHidden = false
  HatchOffset = (0,0,0)
  HatchRotation = 0
  HatchScale = 1
  IsoCount = 0
  IsoHidden = false
  IsoVisible = false
  LockPosition = false
  NameGeomPattern = Diamond
  Perspective = false
  Rotation = 0
  Scale = 3
  ScaleType = 2
  ScrubCount = 0
  SeamHidden = false
  SeamVisible = false
  SectionDirection = 4
  SectionLineStretch = 1
  SectionNormal = (0,-1e-16,-1)
  SectionOrigin = (6,0,-2.5)
  SmoothHidden = false
  SmoothVisible = true
  Source = -> [Cut006_solid]
  TrimAfterCut = false
  UsePreviousCut = false
  X = 79.6226
  XDirection = (0,-1,1e-16)
  Y = 118.575
FEATURE [TechDraw::DrawViewDimension] Dimension037
  AngleOverride = false
  Arbitrary = false
  ArbitraryTolerances = false
  EqualTolerance = true
  ExtensionAngle = 0
  FormatSpec = %.2w
  FormatSpecOverTolerance = %+.2w
  FormatSpecUnderTolerance = %+.2w
  Inverted = false
  LineAngle = 0
  LockPosition = false
  MeasureType = 1
  OverTolerance = 0
  References2D = -> [SectionView002]
  Rotation = 0
  ScaleType = 0
  TheoreticalExact = false
  Type = 0
  UnderTolerance = 0
  X = 0.325776
  Y = -3.69577
FEATURE [TechDraw::DrawViewDimension] Dimension038
  AngleOverride = false
  Arbitrary = false
  ArbitraryTolerances = false
  EqualTolerance = true
  ExtensionAngle = 0
  FormatSpec = %.2w
  FormatSpecOverTolerance = %+.2w
  FormatSpecUnderTolerance = %+.2w
  Inverted = false
  LineAngle = 0
  LockPosition = false
  MeasureType = 1
  OverTolerance = 0
  References2D = -> [SectionView002]
  Rotation = 0
  ScaleType = 0
  TheoreticalExact = false
  Type = 0
  UnderTolerance = 0
  X = 0.255463
  Y = 4.6556
FEATURE [TechDraw::DrawViewDimension] Dimension039
  AngleOverride = false
  Arbitrary = false
  ArbitraryTolerances = false
  EqualTolerance = true
  ExtensionAngle = 0
  FormatSpec = %.2w
  FormatSpecOverTolerance = %+.2w
  FormatSpecUnderTolerance = %+.2w
  Inverted = false
  LineAngle = 0
  LockPosition = false
  MeasureType = 1
  OverTolerance = 0
  References2D = -> [SectionView002]
  Rotation = 0
  ScaleType = 0
  TheoreticalExact = false
  Type = 0
  UnderTolerance = 0
  X = 79.5736
  Y = 0.671184
FEATURE [TechDraw::DrawViewDimension] Dimension040
  AngleOverride = false
  Arbitrary = false
  ArbitraryTolerances = false
  EqualTolerance = true
  ExtensionAngle = 0
  FormatSpec = ⌀%.2w (2x M3)
  FormatSpecOverTolerance = %+.2w
  FormatSpecUnderTolerance = %+.2w
  Inverted = false
  LineAngle = 0
  LockPosition = false
  MeasureType = 1
  OverTolerance = 0
  References2D = -> [SectionView002]
  Rotation = 0
  ScaleType = 0
  TheoreticalExact = false
  Type = 5
  UnderTolerance = 0
  X = 64.4898
  Y = 40.7105
FEATURE [TechDraw::DrawViewDimension] Dimension041
  AngleOverride = false
  Arbitrary = false
  ArbitraryTolerances = false
  EqualTolerance = true
  ExtensionAngle = 0
  FormatSpec = %.2w
  FormatSpecOverTolerance = %+.2w
  FormatSpecUnderTolerance = %+.2w
  Inverted = false
  LineAngle = 0
  LockPosition = false
  MeasureType = 1
  OverTolerance = 0
  References2D = -> [SectionView002]
  Rotation = 0
  ScaleType = 0
  TheoreticalExact = false
  Type = 0
  UnderTolerance = 0
  X = 78.1881
  Y = 8.43953
FEATURE [TechDraw::DrawViewDimension] Dimension042
  AngleOverride = false
  Arbitrary = false
  ArbitraryTolerances = false
  EqualTolerance = true
  ExtensionAngle = 0
  FormatSpec = R%.2w
  FormatSpecOverTolerance = %+.2w
  FormatSpecUnderTolerance = %+.2w
  Inverted = false
  LineAngle = 0
  LockPosition = false
  MeasureType = 1
  OverTolerance = 0
  References2D = -> [SectionView002]
  Rotation = 0
  ScaleType = 0
  TheoreticalExact = false
  Type = 4
  UnderTolerance = 0
  X = -21.5107
  Y = 13.7302
FEATURE [TechDraw::DrawViewDimension] Dimension043
  AngleOverride = false
  Arbitrary = false
  ArbitraryTolerances = false
  EqualTolerance = true
  ExtensionAngle = 0
  FormatSpec = %.2w
  FormatSpecOverTolerance = %+.2w
  FormatSpecUnderTolerance = %+.2w
  Inverted = false
  LineAngle = 0
  LockPosition = false
  MeasureType = 1
  OverTolerance = 0
  References2D = -> [SectionView002]
  Rotation = 0
  ScaleType = 0
  TheoreticalExact = false
  Type = 0
  UnderTolerance = 0
  X = 45.5158
  Y = 34.0796
FEATURE [TechDraw::DrawPage] Page002
  KeepUpdated = true
  NextBalloonIndex = 1
  ProjectionType = 0
  Template = -> Template002
  Views = -> [View,View001,SectionView001,Dimension033,Dimension034,Dimension035,Dimension036,SectionView002,Dimension037,Dimension038,Dimension039,Dimension040,Dimension041,Dimension042,Dimension043]
note: 9 file-system paths scrubbed to <path> (originals preserved in the JSON sidecar)
